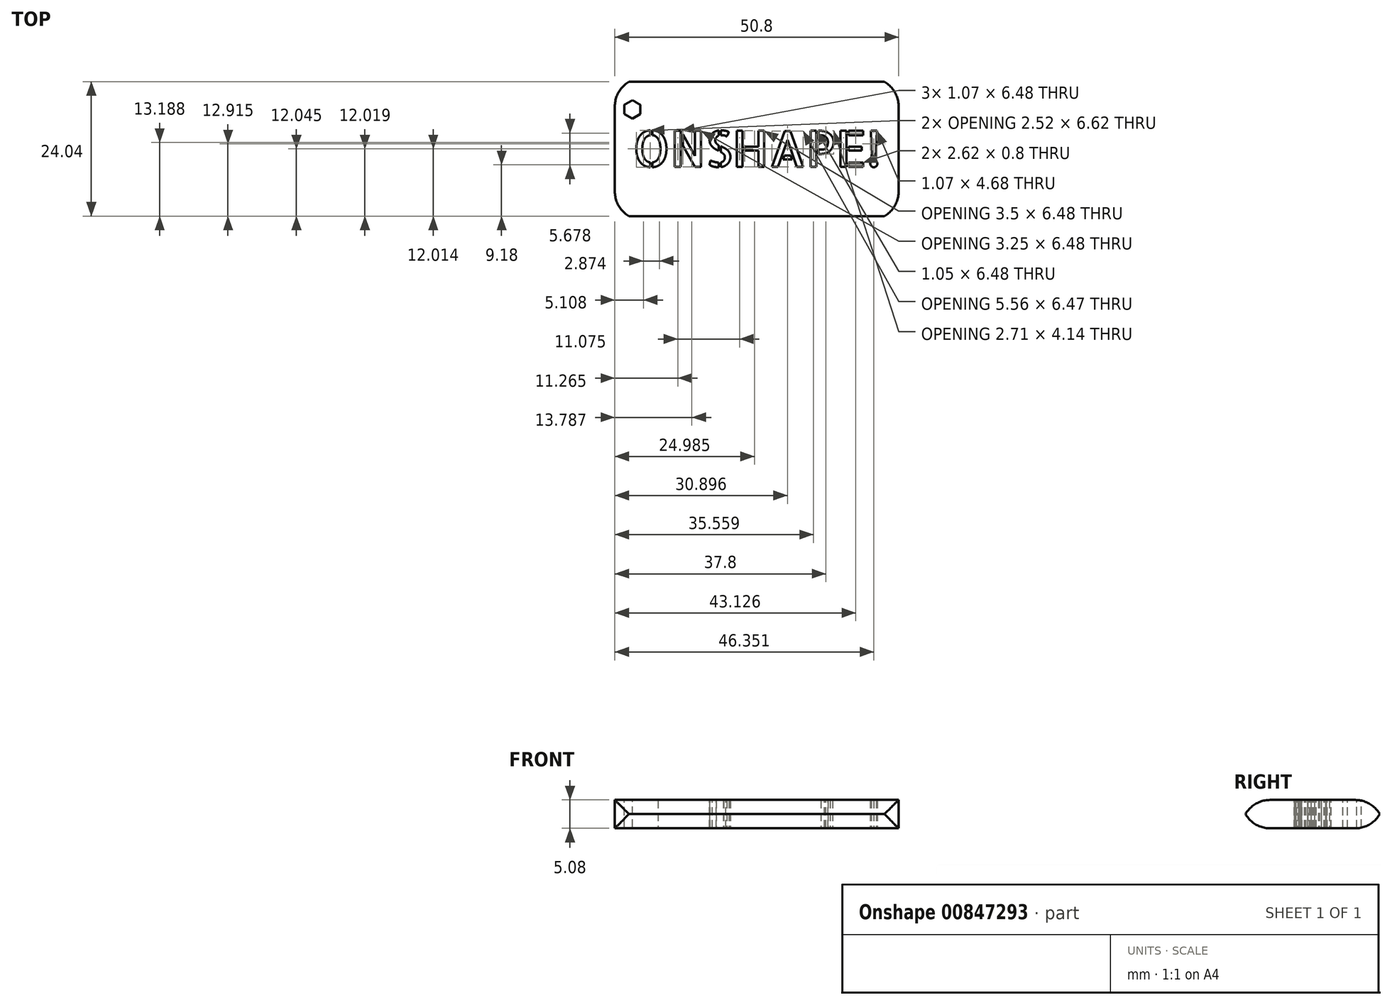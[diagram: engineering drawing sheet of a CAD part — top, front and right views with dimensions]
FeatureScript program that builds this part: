
annotation { "Feature Type Name" : "Feature", "Feature Type Description" : "" }
export const myFeature = defineFeature(function(context is Context, id is Id, definition is map)
    precondition{}
    {
        {
            var Q0;
            Q0=qCreatedBy(makeId("Top.planeOp"),FACE);
            var sketch = newSketch(context, id + "F0", { "sketchPlane" : qUnion([Q0])});
            skLineSegment(sketch, "E0.bottom", {"start": v(25.4, -12.7) * mm, "end": v(-25.4, -12.7) * mm});
            skLineSegment(sketch, "E0.top", {"start": v(25.4, 12.7) * mm, "end": v(-25.4, 12.7) * mm});
            skLineSegment(sketch, "E0.left", {"start": v(25.4, -12.7) * mm, "end": v(25.4, 12.7) * mm});
            skLineSegment(sketch, "E0.right", {"start": v(-25.4, -12.7) * mm, "end": v(-25.4, 12.7) * mm});
            skPoint(sketch, "E0.middle", {"position": v(0, 0) * mm});
            skSolve(sketch);
        }
        {
            var Q0;
            Q0=makeQuery(id+"F0.imprint","IMPRINT",FACE,{"disambiguationData":[TD([[makeQuery(id+"F0.imprint","IMPRINT",EDGE,{"derivedFrom":sQuery(id+"F0.wireOp",EDGE,"E0.bottom")}),-1.0]])]});
            extrude(context, id + "F1", {"entities" : qUnion([Q0]), "depth" : 5.08 * mm, "offsetDistance" : 25.4 * mm});
        }
        {
            var Q0;
            Q0=makeQuery(id+"F1.opExtrude","CAP_FACE",FACE,{"disambiguationData":[OSD([sQuery(id+"F0.wireOp",EDGE,"E0.bottom"),sQuery(id+"F0.wireOp",EDGE,"E0.top"),sQuery(id+"F0.wireOp",EDGE,"E0.left"),sQuery(id+"F0.wireOp",EDGE,"E0.right")])],"isStart":false});
            var sketch = newSketch(context, id + "F2", { "sketchPlane" : qUnion([Q0])});
            skPoint(sketch, "E1", {"position": v(0, 0) * mm});
            skText(sketch, "E2", { "text": "ONSHAPE!", "fontName": "AllertaStencil-Regular.ttf"});
            skCircle(sketch, "E3.cCircle", {"center": v(-22.25, 7.08) * mm, "radius": 1.42 * mm, "construction": true});
            skLineSegment(sketch, "E3.0", {"start": v(-20.82, 7.9) * mm, "end": v(-20.82, 6.26) * mm});
            skLineSegment(sketch, "E3.1", {"start": v(-20.82, 6.26) * mm, "end": v(-22.25, 5.44) * mm});
            skLineSegment(sketch, "E3.2", {"start": v(-22.25, 5.44) * mm, "end": v(-23.67, 6.26) * mm});
            skLineSegment(sketch, "E3.3", {"start": v(-23.67, 6.26) * mm, "end": v(-23.67, 7.9) * mm});
            skLineSegment(sketch, "E3.4", {"start": v(-23.67, 7.9) * mm, "end": v(-22.25, 8.72) * mm});
            skLineSegment(sketch, "E3.5", {"start": v(-22.25, 8.72) * mm, "end": v(-20.82, 7.9) * mm});
            skPoint(sketch, "E3.0.midPoint", {"position": v(-20.82, 7.08) * mm});
            const initialGuessF2  = {"E2": [-0.02223, -0.00324, 1, 0, 0.00648]};
            skSetInitialGuess(sketch, initialGuessF2);
            skSolve(sketch);
        }
        {
            var Q0;
            Q0 = qSketchRegion(id + "F2", true);
            extrude(context, id + "F3", {"entities" : qUnion([Q0]), "operationType" : NewBodyOperationType.REMOVE, "oppositeDirection" : true, "depth" : 25.4 * mm, "offsetDistance" : 25.4 * mm});
        }
        {
            var Q0;
            Q0=makeQuery(id+"F1.opExtrude","SWEPT_EDGE",EDGE,{"disambiguationData":[OSD([sQuery(id+"F0.wireOp",EDGE,"E0.top"),sQuery(id+"F0.wireOp",EDGE,"E0.right")])]});
            var Q1;
            Q1=makeQuery(id+"F1.opExtrude","SWEPT_EDGE",EDGE,{"disambiguationData":[OSD([sQuery(id+"F0.wireOp",EDGE,"E0.bottom"),sQuery(id+"F0.wireOp",EDGE,"E0.right")])]});
            var Q2;
            Q2=makeQuery(id+"F1.opExtrude","SWEPT_EDGE",EDGE,{"disambiguationData":[OSD([sQuery(id+"F0.wireOp",EDGE,"E0.bottom"),sQuery(id+"F0.wireOp",EDGE,"E0.left")])]});
            var Q3;
            Q3=makeQuery(id+"F1.opExtrude","SWEPT_EDGE",EDGE,{"disambiguationData":[OSD([sQuery(id+"F0.wireOp",EDGE,"E0.top"),sQuery(id+"F0.wireOp",EDGE,"E0.left")])]});
            var Q4;
            Q4=makeQuery(id+"F1.opExtrude","CAP_EDGE",EDGE,{"disambiguationData":[OSD([sQuery(id+"F0.wireOp",EDGE,"E0.bottom")])],"isStart":false});
            var Q5;
            Q5=makeQuery(id+"F1.opExtrude","CAP_EDGE",EDGE,{"disambiguationData":[OSD([sQuery(id+"F0.wireOp",EDGE,"E0.bottom")])],"isStart":true});
            var Q6;
            Q6=makeQuery(id+"F1.opExtrude","CAP_EDGE",EDGE,{"disambiguationData":[OSD([sQuery(id+"F0.wireOp",EDGE,"E0.top")])],"isStart":false});
            var Q7;
            Q7=makeQuery(id+"F1.opExtrude","CAP_EDGE",EDGE,{"disambiguationData":[OSD([sQuery(id+"F0.wireOp",EDGE,"E0.top")])],"isStart":true});
            fillet(context, id + "F4", {"entities" : qUnion([Q0, Q1, Q2, Q3, Q4, Q5, Q6, Q7]), "radius" : 5.08 * mm, "tangentPropagation" : true, "allowEdgeOverflow" : false});
        }
    });
